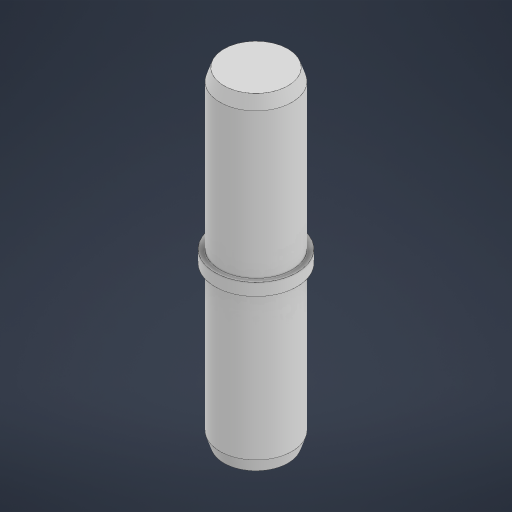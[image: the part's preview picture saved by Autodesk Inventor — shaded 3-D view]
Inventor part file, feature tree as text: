
AUTODESK INVENTOR PART (.ipt)
format: ipt  version: 2023 (Build 270158000, 158)  size: 188,416 bytes
history: native  units: mm
features: chamfer x2, revolve x1, sketch x1
ambient origin geometry x8: Origin, YZ Plane, XZ Plane, XY Plane, X Axis, Y Axis, Z Axis, Center Point
bodies: Solid1 (feature_tree)
feature tree (4):
  revolve  "Revolution1"  [1 undecoded]
  chamfer  "Chamfer1"  Distance=40.0mm
  chamfer  "Chamfer2"  Distance=3.0mm
  sketch  "Sketch2"  dims[d2=8.825mm d3=40.0mm d4=40.0mm d5=3.0mm d6=10.025mm d7=90.0deg d8=1.0mm d9=3.0mm d10=45.0deg d11=3.0mm d12=1.0mm d13=45.0deg]
note: 1 required parameter value undecoded (feature->parameter linkage not recoverable at this tier; creation-order binding heuristic only, values carry confidence <= 0.55)
